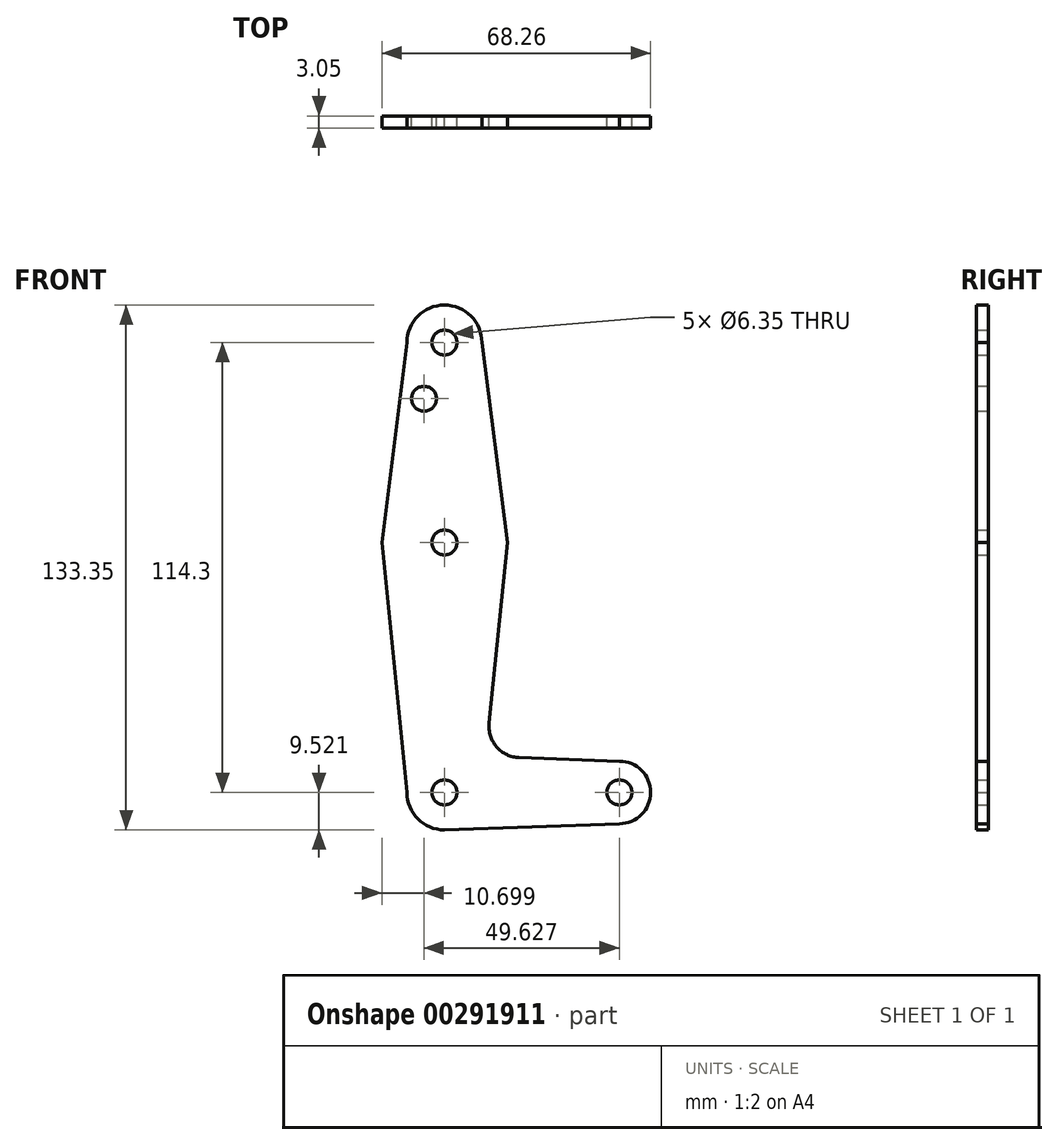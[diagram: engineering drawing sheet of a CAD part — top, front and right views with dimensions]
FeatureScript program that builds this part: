
annotation { "Feature Type Name" : "Feature", "Feature Type Description" : "" }
export const myFeature = defineFeature(function(context is Context, id is Id, definition is map)
    precondition{}
    {
        {
            var Q0;
            Q0=qCreatedBy(makeId("Front.planeOp"),FACE);
            var sketch = newSketch(context, id + "F0", { "sketchPlane" : qUnion([Q0])});
            skCircle(sketch, "E0", {"center": v(-9.33, 68.16) * mm, "radius": 9.53 * mm});
            skCircle(sketch, "E1", {"center": v(-9.33, 17.36) * mm, "radius": 15.88 * mm});
            skCircle(sketch, "E2", {"center": v(-9.33, -46.14) * mm, "radius": 9.53 * mm});
            skCircle(sketch, "E3", {"center": v(35.12, -46.14) * mm, "radius": 7.94 * mm});
            skLineSegment(sketch, "E4", {"start": v(-18.86, 68.16) * mm, "end": v(-25.2, 17.36) * mm});
            skLineSegment(sketch, "E5", {"start": v(0.2, 68.16) * mm, "end": v(6.67, 17.36) * mm});
            skLineSegment(sketch, "E6", {"start": v(-25.2, 17.36) * mm, "end": v(-18.86, -46.14) * mm});
            skLineSegment(sketch, "E7", {"start": v(6.67, 17.36) * mm, "end": v(2.02, -28.55) * mm});
            skLineSegment(sketch, "E8", {"start": v(9.65, -37.3) * mm, "end": v(35.12, -38.2) * mm});
            skLineSegment(sketch, "E9", {"start": v(-9.33, -55.66) * mm, "end": v(35.12, -54.08) * mm});
            skPoint(sketch, "E10.newPointA", {"position": v(0.24, -46.14) * mm});
            skPoint(sketch, "E10.newPointB", {"position": v(-9.33, -36.61) * mm});
            skArc(sketch, "E10.filletArc", {"start": v(2.02, -28.55) * mm, "mid": v(3.94, -34.57) * mm, "end": v(9.65, -37.3) * mm});
            skLineSegment(sketch, "E11", {"start": v(-9.33, 68.16) * mm, "end": v(-9.33, 17.36) * mm, "construction": true});
            skCircle(sketch, "E12", {"center": v(-14.51, 53.89) * mm, "radius": 3.18 * mm});
            skCircle(sketch, "E13", {"center": v(-9.33, 68.16) * mm, "radius": 3.18 * mm});
            skCircle(sketch, "E14", {"center": v(-9.33, 17.36) * mm, "radius": 3.18 * mm});
            skCircle(sketch, "E15", {"center": v(-9.33, -46.14) * mm, "radius": 3.18 * mm});
            skCircle(sketch, "E16", {"center": v(35.12, -46.14) * mm, "radius": 3.18 * mm});
            skLineSegment(sketch, "E17", {"start": v(-9.33, 17.36) * mm, "end": v(-9.33, -46.14) * mm, "construction": true});
            skLineSegment(sketch, "E18", {"start": v(-9.33, -46.14) * mm, "end": v(35.12, -46.14) * mm, "construction": true});
            skSolve(sketch);
        }
        {
            var Q0;
            Q0=makeQuery(id+"F0.imprint","IMPRINT",FACE,{"disambiguationData":[TD([[makeQuery(id+"F0.imprint","IMPRINT",EDGE,{"derivedFrom":sQuery(id+"F0.wireOp",EDGE,"E12")}),-1.0]])]});
            var Q1;
            Q1=makeQuery(id+"F0.imprint","IMPRINT",FACE,{"disambiguationData":[TD([[makeQuery(id+"F0.imprint","IMPRINT",EDGE,{"derivedFrom":sQuery(id+"F0.wireOp",EDGE,"E13")}),-1.0]])]});
            var Q2;
            Q2=makeQuery(id+"F0.imprint","IMPRINT",FACE,{"disambiguationData":[TD([[makeQuery(id+"F0.imprint","IMPRINT",EDGE,{"derivedFrom":sQuery(id+"F0.wireOp",EDGE,"E14")}),-1.0]])]});
            var Q3;
            {var subQ0=sQuery(id+"F0.wireOp",EDGE,"E7");Q3=makeQuery(id+"F0.imprint","IMPRINT",FACE,{"disambiguationData":[TD([[makeQuery(id+"F0.imprint","IMPRINT",EDGE,{"derivedFrom":subQ0}),-1.0]])]});}
            var Q4;
            Q4=makeQuery(id+"F0.imprint","IMPRINT",FACE,{"disambiguationData":[TD([[makeQuery(id+"F0.imprint","IMPRINT",EDGE,{"derivedFrom":sQuery(id+"F0.wireOp",EDGE,"E15")}),-1.0]])]});
            var Q5;
            Q5=makeQuery(id+"F0.imprint","IMPRINT",FACE,{"disambiguationData":[TD([[makeQuery(id+"F0.imprint","IMPRINT",EDGE,{"derivedFrom":sQuery(id+"F0.wireOp",EDGE,"E16")}),-1.0]])]});
            extrude(context, id + "F1", {"entities" : qUnion([Q0, Q1, Q2, Q3, Q4, Q5]), "depth" : 3.05 * mm});
        }
    });
